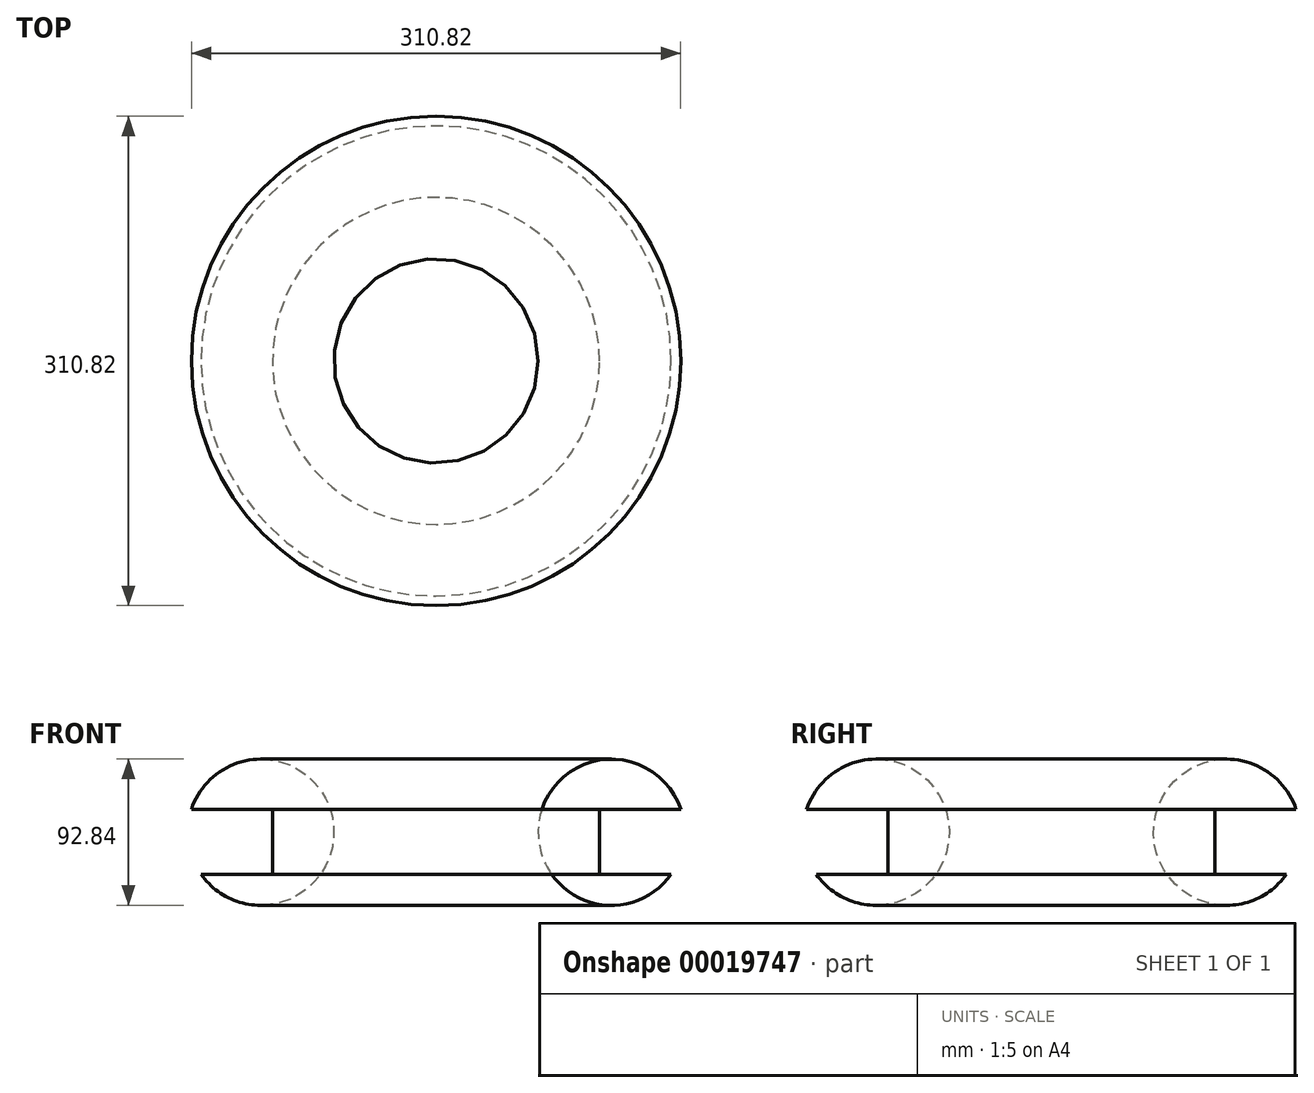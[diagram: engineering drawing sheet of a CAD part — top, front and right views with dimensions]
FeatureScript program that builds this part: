
annotation { "Feature Type Name" : "Feature", "Feature Type Description" : "" }
export const myFeature = defineFeature(function(context is Context, id is Id, definition is map)
    precondition{}
    {
        {
            var Q0;
            Q0=qCreatedBy(makeId("Front.planeOp"),FACE);
            var sketch = newSketch(context, id + "F0", { "sketchPlane" : qUnion([Q0])});
            skCircle(sketch, "E0", {"center": v(111.3, 0) * mm, "radius": 46.42 * mm});
            skSolve(sketch);
        }
        {
            var Q0;
            Q0=qCreatedBy(makeId("Front.planeOp"),FACE);
            var sketch = newSketch(context, id + "F1", { "sketchPlane" : qUnion([Q0])});
            skLineSegment(sketch, "E1", {"start": v(0, 76.47) * mm, "end": v(0, -77.6) * mm, "construction": true});
            skSolve(sketch);
        }
        {
            var Q0;
            Q0 = qSketchRegion(id + "F0", true);
            var Q1;
            Q1=sQuery(id+"F1.wireOp",EDGE,"E1");
            revolve(context, id + "F2", {"entities" : qUnion([Q0]), "axis" : qUnion([Q1]), "revolveType" : RevolveType.FULL});
        }
        {
            var Q0;
            Q0=qCreatedBy(makeId("Front.planeOp"),FACE);
            var sketch = newSketch(context, id + "F3", { "sketchPlane" : qUnion([Q0])});
            skLineSegment(sketch, "E2.bottom", {"start": v(103.87, 14.47) * mm, "end": v(167.9, 14.47) * mm});
            skLineSegment(sketch, "E2.top", {"start": v(103.87, -26.73) * mm, "end": v(167.9, -26.73) * mm});
            skLineSegment(sketch, "E2.left", {"start": v(103.87, 14.47) * mm, "end": v(103.87, -26.73) * mm});
            skLineSegment(sketch, "E2.right", {"start": v(167.9, 14.47) * mm, "end": v(167.9, -26.73) * mm});
            skLineSegment(sketch, "E3", {"start": v(0, -55.34) * mm, "end": v(0, 50.57) * mm, "construction": true});
            skSolve(sketch);
        }
        {
            var Q0;
            Q0=makeQuery(id+"F3.imprint","IMPRINT",FACE,{"disambiguationData":[TD([[makeQuery(id+"F3.imprint","IMPRINT",EDGE,{"derivedFrom":sQuery(id+"F3.wireOp",EDGE,"E2.bottom")}),-1.0]])]});
            var Q1;
            Q1=sQuery(id+"F3.wireOp",EDGE,"E3");
            revolve(context, id + "F4", {"operationType" : NewBodyOperationType.REMOVE, "entities" : qUnion([Q0]), "axis" : qUnion([Q1]), "revolveType" : RevolveType.FULL, "oppositeDirection" : true});
        }
    });
